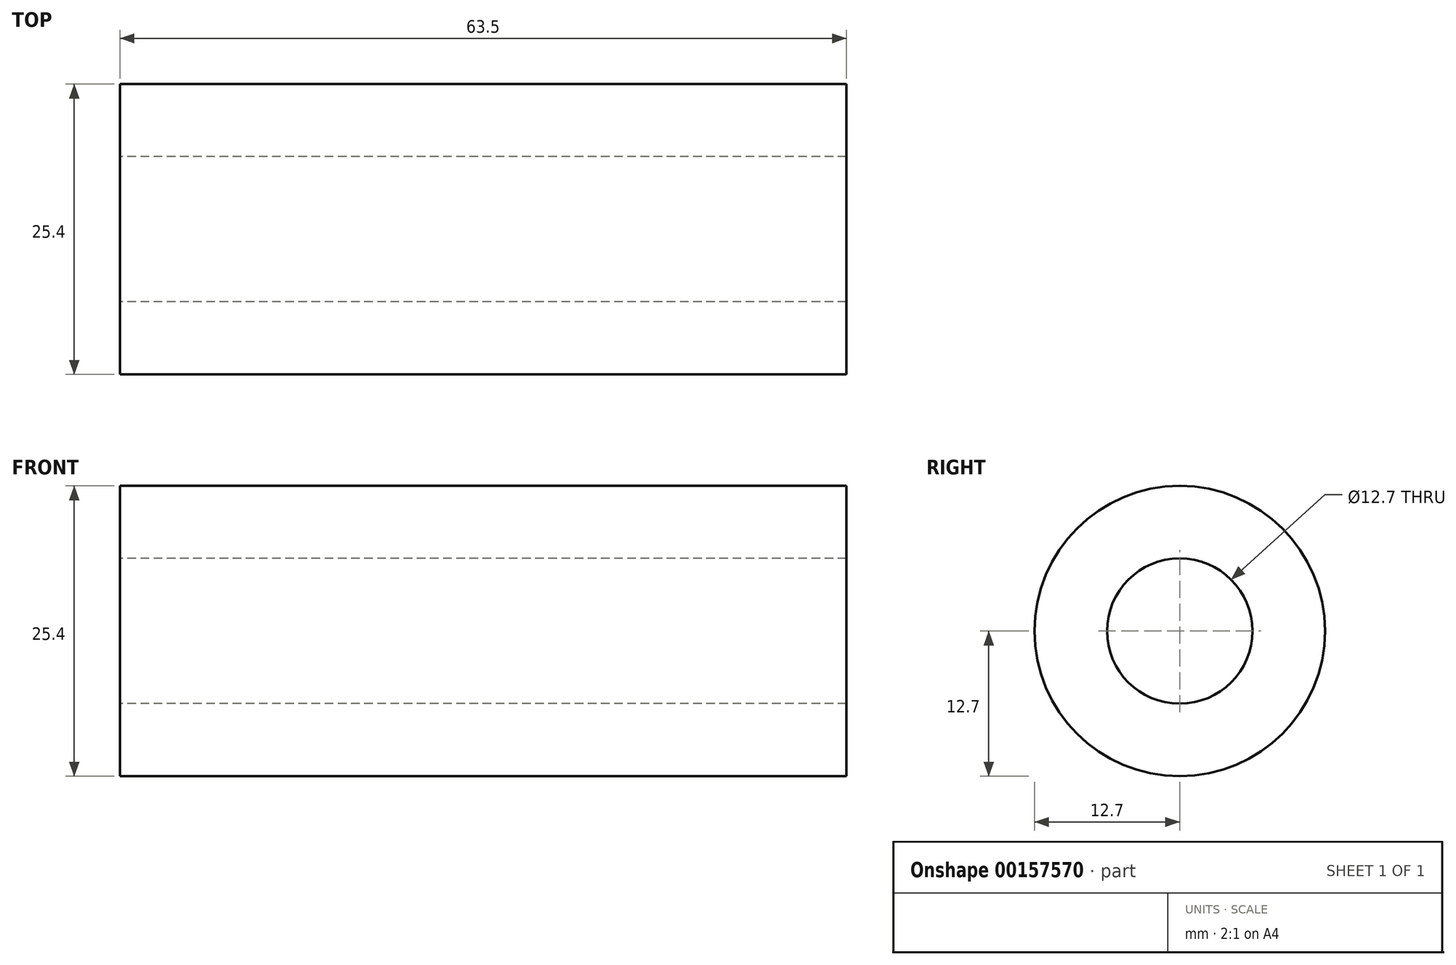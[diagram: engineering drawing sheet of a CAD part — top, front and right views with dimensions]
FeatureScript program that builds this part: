
annotation { "Feature Type Name" : "Feature", "Feature Type Description" : "" }
export const myFeature = defineFeature(function(context is Context, id is Id, definition is map)
    precondition{}
    {
        {
            var Q0;
            Q0=qCreatedBy(makeId("Right.planeOp"),FACE);
            var sketch = newSketch(context, id + "F0", { "sketchPlane" : qUnion([Q0])});
            skCircle(sketch, "E0", {"center": v(0, 0) * mm, "radius": 12.7 * mm});
            skCircle(sketch, "E1", {"center": v(0, 0) * mm, "radius": 6.35 * mm});
            skLineSegment(sketch, "E2", {"start": v(0, 0) * mm, "end": v(52.9, -35.12) * mm, "construction": true});
            skSolve(sketch);
        }
        {
            var Q0;
            Q0=makeQuery(id+"F0.imprint","IMPRINT",FACE,{"disambiguationData":[TD([[makeQuery(id+"F0.imprint","IMPRINT",EDGE,{"derivedFrom":sQuery(id+"F0.wireOp",EDGE,"E0")}),1.0]])]});
            extrude(context, id + "F1", {"entities" : qUnion([Q0]), "depth" : 63.5 * mm});
        }
    });
